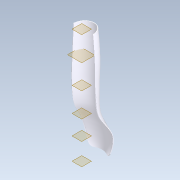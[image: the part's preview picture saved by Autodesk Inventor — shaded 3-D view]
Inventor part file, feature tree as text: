
AUTODESK INVENTOR PART (.ipt)
format: ipt  version: 2020.2 (Build 242310000, 310)  size: 477,184 bytes
history: native  units: mm
features: plane x6, sketch x6, fillet x2, loft x1
ambient origin geometry x8: Origin, YZ Plane, XZ Plane, XY Plane, X Axis, Y Axis, Z Axis, Center Point
bodies: Solid1 (feature_tree)
feature tree (15):
  plane  "Work Plane6"
  loft  "Loft1"
  fillet  "Fillet2"  [1 undecoded]
  fillet  "Fillet3"  [1 undecoded]
  plane  "Work Plane1"
  plane  "Work Plane2"
  plane  "Work Plane3"
  plane  "Work Plane4"
  plane  "Work Plane5"
  sketch  "Sketch1"  dims[d0=-30.0mm d1=-50.0mm d2=-50.0mm d3=-50.0mm]
  sketch  "Sketch2"  dims[d4=-40.0mm d5=-45.0mm]
  sketch  "Sketch3"  dims[d10=1.0mm]
  sketch  "Sketch4"  dims[d11=1.0mm]
  sketch  "Sketch5"  dims[d12=1.0mm]
  sketch  "Sketch6"  dims[d13=1.0mm d14=0.0mm d15=90.0deg d16=0.0mm d17=90.0deg d18=0.0mm d19=90.0deg d20=0.0mm d21=90.0deg d22=0.0mm d23=90.0deg d24=0.0mm d25=90.0deg d27=1.0mm d29=1.0mm d30=10.0mm d31=5.0mm]
note: 2 required parameter values undecoded (feature->parameter linkage not recoverable at this tier; creation-order binding heuristic only, values carry confidence <= 0.55)
